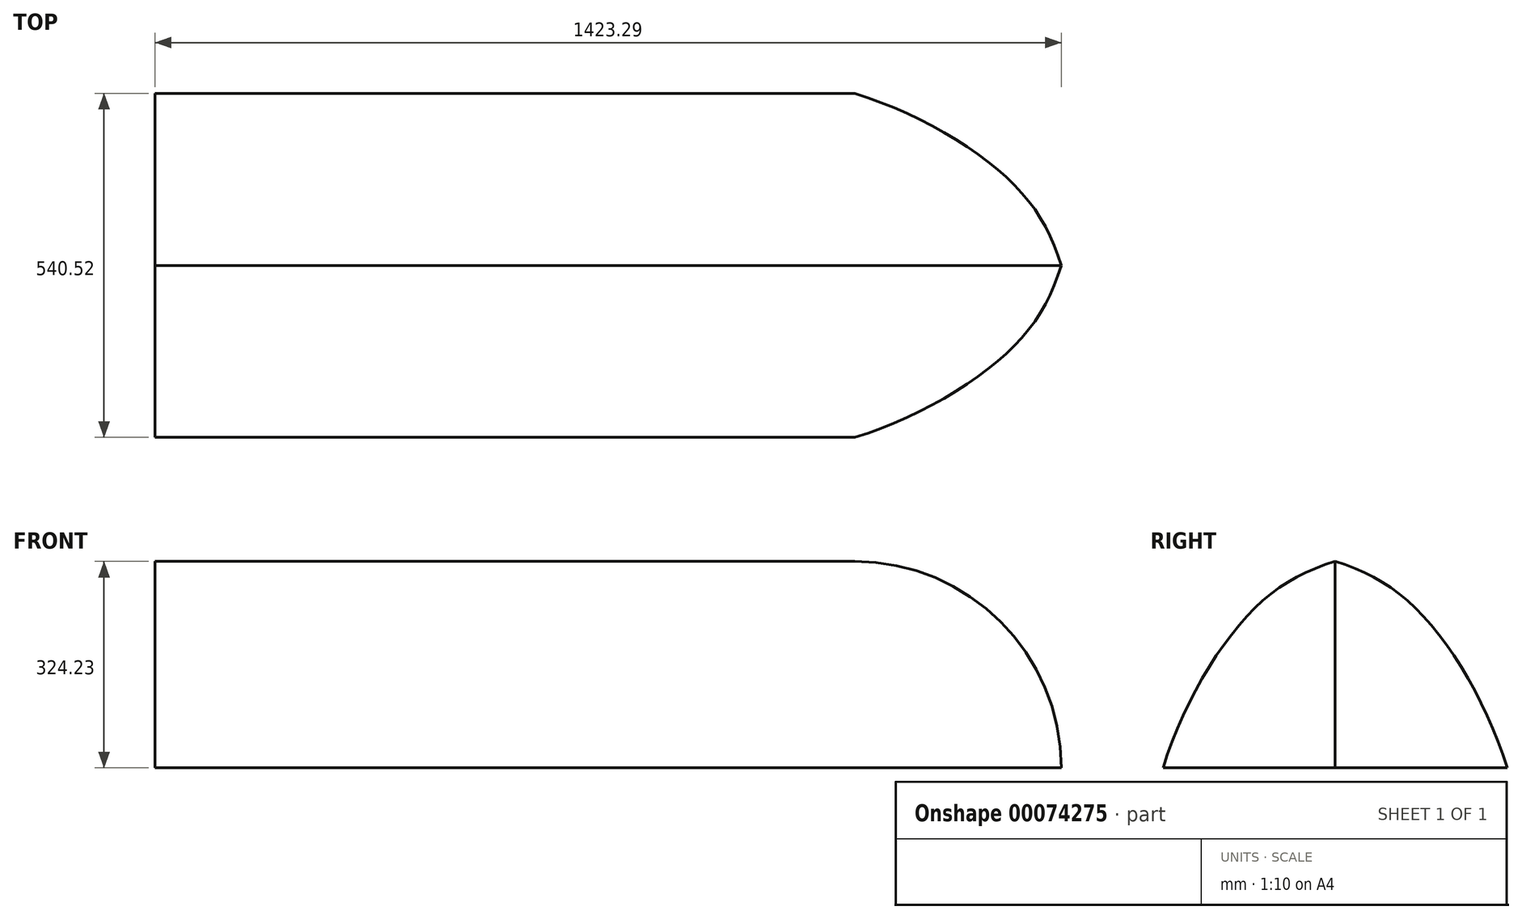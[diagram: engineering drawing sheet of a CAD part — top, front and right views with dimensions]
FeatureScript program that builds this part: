
annotation { "Feature Type Name" : "Feature", "Feature Type Description" : "" }
export const myFeature = defineFeature(function(context is Context, id is Id, definition is map)
    precondition{}
    {
        {
            var Q0;
            Q0=qCreatedBy(makeId("Top.planeOp"),FACE);
            var sketch = newSketch(context, id + "F0", { "sketchPlane" : qUnion([Q0])});
            skPoint(sketch, "E0.rect.middle", {"position": v(0, 0) * mm});
            skLineSegment(sketch, "E1", {"start": v(-746.5, 0) * mm, "end": v(338.63, 0) * mm, "construction": true});
            skLineSegment(sketch, "E2", {"start": v(-1271.47, 0) * mm, "end": v(1216.55, 0) * mm, "construction": true});
            skFitSpline(sketch, "E3", {"points": [v(1043.08, 0) * mm, v(955.89, -139.48) * mm, v(718.85, -270.26) * mm, v(361.93, -302.96) * mm, v(-624.38, -245.74) * mm, v(-1409.07, 0) * mm], "startDerivative": vector(-414.2, -1394.06) * mm, "endDerivative": vector(-2753.55, 1093.05) * mm});
            skFitSpline(sketch, "E4.MirrorCS", {"points": [v(1043.08, 0) * mm, v(955.89, 139.48) * mm, v(718.85, 270.26) * mm, v(361.93, 302.96) * mm, v(-624.38, 245.74) * mm, v(-1409.07, 0) * mm], "startDerivative": vector(-414.2, 1394.06) * mm, "endDerivative": vector(-2753.55, -1093.05) * mm});
            skLineSegment(sketch, "E5", {"start": v(718.85, -270.26) * mm, "end": v(718.85, 270.26) * mm});
            skSolve(sketch);
        }
        {
            var Q0;
            {var subQ3=sQuery(id+"F0.wireOp",EDGE,"E5");Q0=makeQuery(id+"F0.imprint","IMPRINT",FACE,{"disambiguationData":[TD([[makeQuery(id+"F0.imprint","IMPRINT",EDGE,{"derivedFrom":subQ3}),-1.0]])]});}
            var Q1;
            Q1=sQuery(id+"F0.wireOp",EDGE,"E5");
            revolve(context, id + "F1", {"entities" : qUnion([Q0]), "axis" : qUnion([Q1]), "revolveType" : RevolveType.ONE_DIRECTION, "oppositeDirection" : true, "angle" : 90 * degree});
        }
        {
            var Q0;
            Q0=makeQuery(id+"F1.opRevolve","CAP_FACE",FACE,{"disambiguationData":[OSD([sQuery(id+"F0.wireOp",EDGE,"E3"),sQuery(id+"F0.wireOp",EDGE,"E4.MirrorCS"),sQuery(id+"F0.wireOp",EDGE,"E5")])],"isStart":false});
            var sketch = newSketch(context, id + "F2", { "sketchPlane" : qUnion([Q0])});
            skSolve(sketch);
        }
        {
            var Q0;
            Q0=makeQuery(id+"F2.imprint","IMPRINT",FACE,{"disambiguationData":[TD([[makeQuery(id+"F2.imprint","IMPRINT",EDGE,{"derivedFrom":makeQuery(id+"F1.opRevolve","CAP_EDGE",EDGE,{"disambiguationData":[OSD([sQuery(id+"F0.wireOp",EDGE,"E3")])],"isStart":false})}),-1.0]])]});
            extrude(context, id + "F3", {"entities" : qUnion([Q0]), "operationType" : NewBodyOperationType.ADD, "depth" : 1099.06 * mm});
        }
    });
